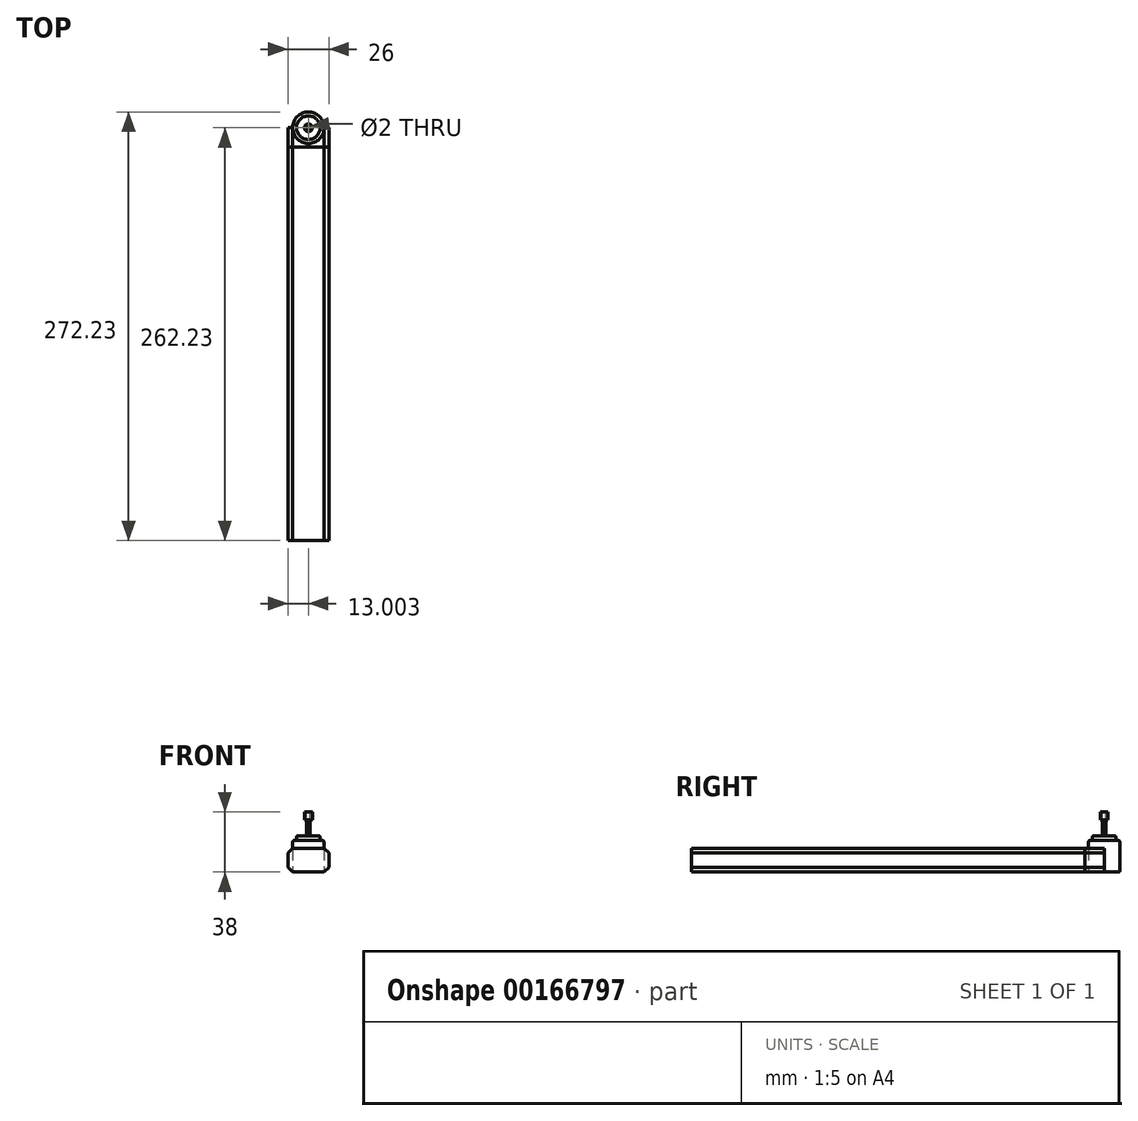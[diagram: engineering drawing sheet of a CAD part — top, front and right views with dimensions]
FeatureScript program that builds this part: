
annotation { "Feature Type Name" : "Feature", "Feature Type Description" : "" }
export const myFeature = defineFeature(function(context is Context, id is Id, definition is map)
    precondition{}
    {
        {
            var Q0;
            Q0=qCreatedBy(makeId("Top.planeOp"),FACE);
            var sketch = newSketch(context, id + "F0", { "sketchPlane" : qUnion([Q0])});
            skCircle(sketch, "E0", {"center": v(-51.09, 0) * mm, "radius": 10 * mm});
            skSolve(sketch);
        }
        {
            var Q0;
            Q0=makeQuery(id+"F0.imprint","IMPRINT",FACE,{"disambiguationData":[TD([[makeQuery(id+"F0.imprint","IMPRINT",EDGE,{"derivedFrom":sQuery(id+"F0.wireOp",EDGE,"E0")}),1.0]])]});
            extrude(context, id + "F1", {"entities" : qUnion([Q0]), "depth" : 20 * mm});
        }
        {
            var Q0;
            Q0=makeQuery(id+"F1.opExtrude","CAP_FACE",FACE,{"disambiguationData":[OSD([sQuery(id+"F0.wireOp",EDGE,"E0")])],"isStart":false});
            var sketch = newSketch(context, id + "F2", { "sketchPlane" : qUnion([Q0])});
            skCircle(sketch, "E1.0.0", {"center": v(-51.09, 0) * mm, "radius": 10 * mm});
            skCircle(sketch, "E2", {"center": v(-51.09, 0) * mm, "radius": 7.5 * mm});
            skSolve(sketch);
        }
        {
            var Q0;
            Q0=makeQuery(id+"F2.imprint","IMPRINT",FACE,{"disambiguationData":[TD([[makeQuery(id+"F2.imprint","IMPRINT",EDGE,{"derivedFrom":sQuery(id+"F2.wireOp",EDGE,"E2")}),1.0]])]});
            extrude(context, id + "F3", {"entities" : qUnion([Q0]), "operationType" : NewBodyOperationType.ADD, "depth" : 3 * mm});
        }
        {
            var Q0;
            Q0=makeQuery(id+"F3.opExtrude","CAP_FACE",FACE,{"disambiguationData":[OSD([sQuery(id+"F2.wireOp",EDGE,"E2")])],"isStart":false});
            var sketch = newSketch(context, id + "F4", { "sketchPlane" : qUnion([Q0])});
            skCircle(sketch, "E3.0.0", {"center": v(-51.09, 0) * mm, "radius": 7.5 * mm});
            skCircle(sketch, "E4", {"center": v(-51.09, 0) * mm, "radius": 1 * mm});
            skSolve(sketch);
        }
        {
            var Q0;
            Q0=makeQuery(id+"F4.imprint","IMPRINT",FACE,{"disambiguationData":[TD([[makeQuery(id+"F4.imprint","IMPRINT",EDGE,{"derivedFrom":sQuery(id+"F4.wireOp",EDGE,"E4")}),1.0]])]});
            extrude(context, id + "F5", {"entities" : qUnion([Q0]), "operationType" : NewBodyOperationType.ADD, "depth" : 15 * mm});
        }
        {
            var Q0;
            Q0=makeQuery(id+"F5.opExtrude","CAP_FACE",FACE,{"disambiguationData":[OSD([sQuery(id+"F4.wireOp",EDGE,"E4")])],"isStart":false});
            var sketch = newSketch(context, id + "F6", { "sketchPlane" : qUnion([Q0])});
            skCircle(sketch, "E5.0", {"center": v(-51.09, 0) * mm, "radius": 1 * mm});
            skCircle(sketch, "E6", {"center": v(-51.09, 0) * mm, "radius": 2.5 * mm});
            skSolve(sketch);
        }
        {
            var Q0;
            Q0=makeQuery(id+"F6.imprint","IMPRINT",FACE,{"disambiguationData":[TD([[makeQuery(id+"F6.imprint","IMPRINT",EDGE,{"derivedFrom":sQuery(id+"F6.wireOp",EDGE,"E5.0")}),-1.0]])]});
            extrude(context, id + "F7", {"entities" : qUnion([Q0]), "oppositeDirection" : true, "depth" : 5 * mm});
        }
        {
            var Q0;
            Q0=makeQuery(id+"F1.opExtrude","CAP_EDGE",EDGE,{"disambiguationData":[OSD([sQuery(id+"F0.wireOp",EDGE,"E0")])],"isStart":true});
            var Q1;
            Q1=makeQuery(id+"F1.opExtrude","CAP_EDGE",EDGE,{"disambiguationData":[OSD([sQuery(id+"F0.wireOp",EDGE,"E0")])],"isStart":false});
            var Q2;
            Q2=makeQuery(id+"F3.opExtrude","CAP_EDGE",EDGE,{"disambiguationData":[OSD([sQuery(id+"F2.wireOp",EDGE,"E2")])],"isStart":false});
            fillet(context, id + "F8", {"entities" : qUnion([Q0, Q1, Q2]), "radius" : 1 * mm, "tangentPropagation" : true, "allowEdgeOverflow" : false});
        }
        {
            var Q0;
            Q0=qCreatedBy(makeId("Top.planeOp"),FACE);
            var sketch = newSketch(context, id + "F9", { "sketchPlane" : qUnion([Q0])});
            skCircle(sketch, "E7.0", {"center": v(-51.09, 0) * mm, "radius": 10 * mm});
            skArc(sketch, "E8", {"start": v(-61.09, 0) * mm, "mid": v(-51.09, -10) * mm, "end": v(-41.09, 0) * mm});
            skLineSegment(sketch, "E9", {"start": v(-61.09, 0) * mm, "end": v(-64.09, 0) * mm});
            skLineSegment(sketch, "E10", {"start": v(-64.09, 0) * mm, "end": v(-64.09, -12.23) * mm});
            skLineSegment(sketch, "E11", {"start": v(-64.09, -12.23) * mm, "end": v(-38.09, -12.23) * mm});
            skLineSegment(sketch, "E12", {"start": v(-38.09, -12.23) * mm, "end": v(-38.09, 0) * mm});
            skLineSegment(sketch, "E13", {"start": v(-38.09, 0) * mm, "end": v(-41.09, 0) * mm});
            skLineSegment(sketch, "E14", {"start": v(-51.09, 0) * mm, "end": v(-51.09, 15.36) * mm, "construction": true});
            skLineSegment(sketch, "E15", {"start": v(-64.09, -12.23) * mm, "end": v(-64.09, -262.23) * mm});
            skLineSegment(sketch, "E16", {"start": v(-64.09, -262.23) * mm, "end": v(-38.09, -262.23) * mm});
            skLineSegment(sketch, "E17", {"start": v(-38.09, -262.23) * mm, "end": v(-38.09, -12.23) * mm});
            skSolve(sketch);
        }
        {
            var Q0;
            {var subQ0=sQuery(id+"F9.wireOp",EDGE,"E9");Q0=makeQuery(id+"F9.imprint","IMPRINT",FACE,{"disambiguationData":[TD([[makeQuery(id+"F9.imprint","IMPRINT",EDGE,{"derivedFrom":subQ0}),1.0]])]});}
            extrude(context, id + "F10", {"entities" : qUnion([Q0]), "depth" : 15 * mm});
        }
        {
            var Q0;
            Q0=makeQuery(id+"F9.imprint","IMPRINT",FACE,{"disambiguationData":[TD([[makeQuery(id+"F9.imprint","IMPRINT",EDGE,{"derivedFrom":sQuery(id+"F9.wireOp",EDGE,"E11")}),-1.0]])]});
            extrude(context, id + "F11", {"entities" : qUnion([Q0]), "depth" : 15 * mm});
        }
        {
            var Q0;
            Q0=makeQuery(id+"F11.boolean.opBoolean","MERGE",EDGE,{"derivedFrom":[makeQuery(id+"F10.opExtrude","CAP_EDGE",EDGE,{"disambiguationData":[OSD([sQuery(id+"F9.wireOp",EDGE,"E10")])],"isStart":false}),makeQuery(id+"F11.opExtrude","CAP_EDGE",EDGE,{"disambiguationData":[OSD([sQuery(id+"F9.wireOp",EDGE,"E15")])],"isStart":false})]});
            var Q1;
            Q1=makeQuery(id+"F11.boolean.opBoolean","MERGE",EDGE,{"derivedFrom":[makeQuery(id+"F10.opExtrude","CAP_EDGE",EDGE,{"disambiguationData":[OSD([sQuery(id+"F9.wireOp",EDGE,"E12")])],"isStart":false}),makeQuery(id+"F11.opExtrude","CAP_EDGE",EDGE,{"disambiguationData":[OSD([sQuery(id+"F9.wireOp",EDGE,"E17")])],"isStart":false})]});
            var Q2;
            Q2=makeQuery(id+"F11.boolean.opBoolean","MERGE",EDGE,{"derivedFrom":[makeQuery(id+"F10.opExtrude","CAP_EDGE",EDGE,{"disambiguationData":[OSD([sQuery(id+"F9.wireOp",EDGE,"E12")])],"isStart":true}),makeQuery(id+"F11.opExtrude","CAP_EDGE",EDGE,{"disambiguationData":[OSD([sQuery(id+"F9.wireOp",EDGE,"E17")])],"isStart":true})]});
            var Q3;
            Q3=makeQuery(id+"F11.boolean.opBoolean","MERGE",EDGE,{"derivedFrom":[makeQuery(id+"F10.opExtrude","CAP_EDGE",EDGE,{"disambiguationData":[OSD([sQuery(id+"F9.wireOp",EDGE,"E10")])],"isStart":true}),makeQuery(id+"F11.opExtrude","CAP_EDGE",EDGE,{"disambiguationData":[OSD([sQuery(id+"F9.wireOp",EDGE,"E15")])],"isStart":true})]});
            chamfer(context, id + "F12", {"entities" : qUnion([Q0, Q1, Q2, Q3]), "width" : 3 * mm, "tangentPropagation" : true});
        }
    });
